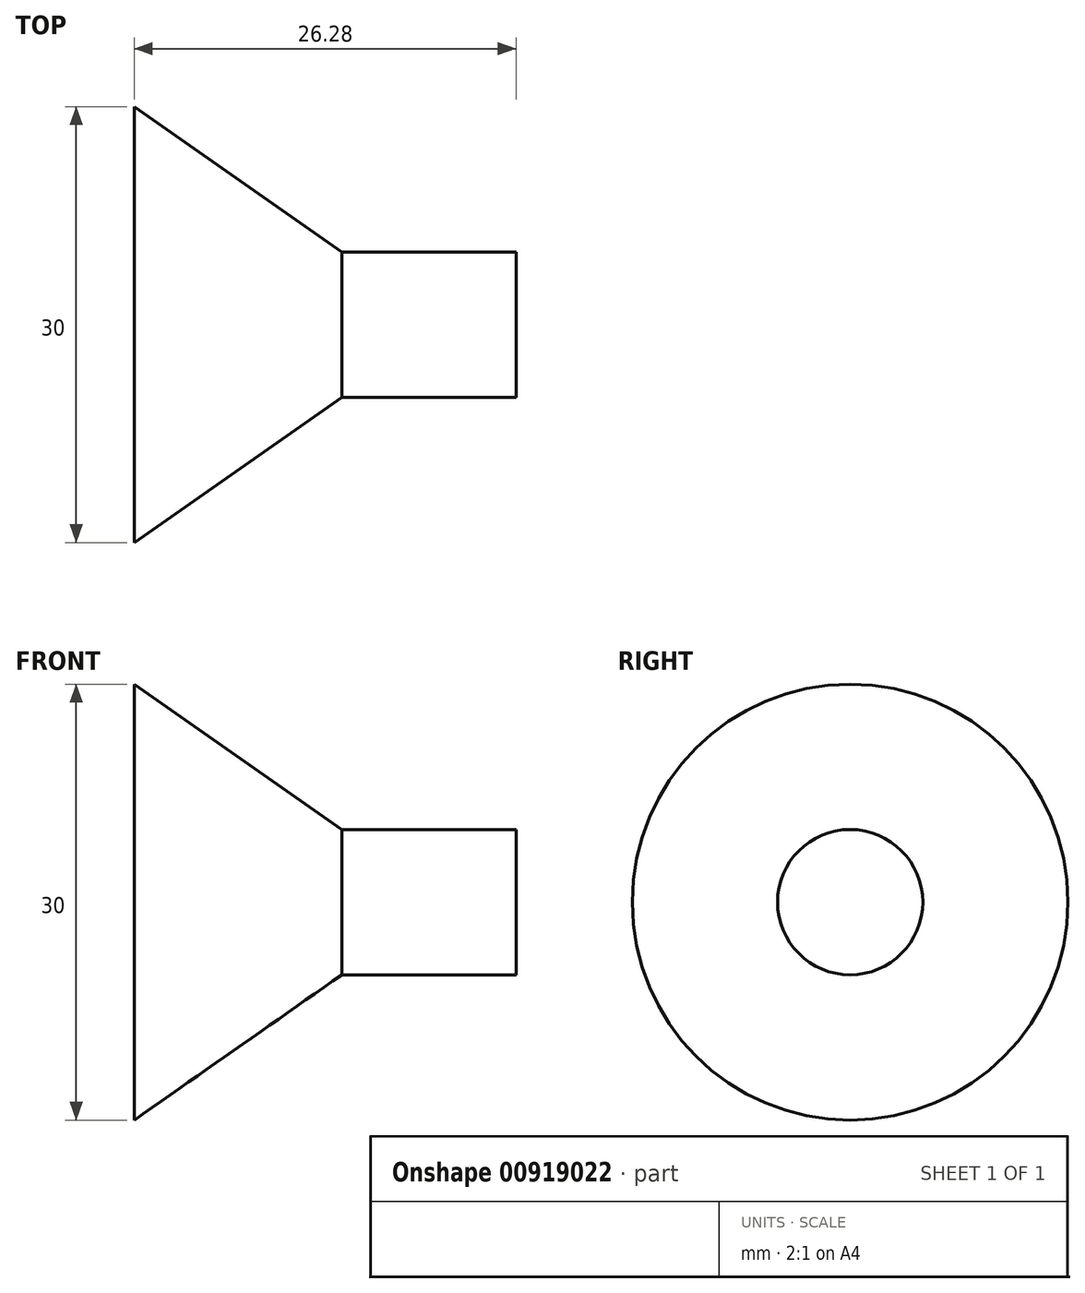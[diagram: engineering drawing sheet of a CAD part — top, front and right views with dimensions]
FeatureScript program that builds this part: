
annotation { "Feature Type Name" : "Feature", "Feature Type Description" : "" }
export const myFeature = defineFeature(function(context is Context, id is Id, definition is map)
    precondition{}
    {
        {
            var Q0;
            Q0=qCreatedBy(makeId("Top.planeOp"),FACE);
            var sketch = newSketch(context, id + "F0", { "sketchPlane" : qUnion([Q0])});
            skLineSegment(sketch, "E0", {"start": v(-14.28, 15) * mm, "end": v(0, 5) * mm});
            skLineSegment(sketch, "E1", {"start": v(0, 0) * mm, "end": v(-14.28, 0) * mm});
            skLineSegment(sketch, "E2", {"start": v(-14.28, 0) * mm, "end": v(-14.28, 15) * mm});
            skLineSegment(sketch, "E3", {"start": v(0, 5) * mm, "end": v(0, 0) * mm});
            skSolve(sketch);
        }
        {
            var Q0;
            Q0=makeQuery(id+"F0.imprint","IMPRINT",FACE,{"disambiguationData":[TD([[makeQuery(id+"F0.imprint","IMPRINT",EDGE,{"derivedFrom":sQuery(id+"F0.wireOp",EDGE,"E0")}),-1.0]])]});
            var Q1;
            {var subQ0=sQuery(id+"F0.wireOp",EDGE,"E1");Q1=makeQuery(id+"F0.imprint","IMPRINT",FACE,{"disambiguationData":[TD([[makeQuery(id+"F0.imprint","IMPRINT",EDGE,{"derivedFrom":subQ0}),-1.0]])]});}
            var Q2;
            Q2=sQuery(id+"F0.wireOp",EDGE,"E1");
            revolve(context, id + "F1", {"surfaceOperationType" : NewSurfaceOperationType.NEW, "entities" : qUnion([Q0, Q1]), "axis" : qUnion([Q2]), "revolveType" : RevolveType.FULL});
        }
        {
            var Q0;
            Q0=makeQuery(id+"F1.opRevolve","SWEPT_FACE",FACE,{"disambiguationData":[OSD([sQuery(id+"F0.wireOp",EDGE,"E3")])]});
            extrude(context, id + "F2", {"entities" : qUnion([Q0]), "operationType" : NewBodyOperationType.ADD, "depth" : 12 * mm, "offsetDistance" : 25 * mm});
        }
    });
